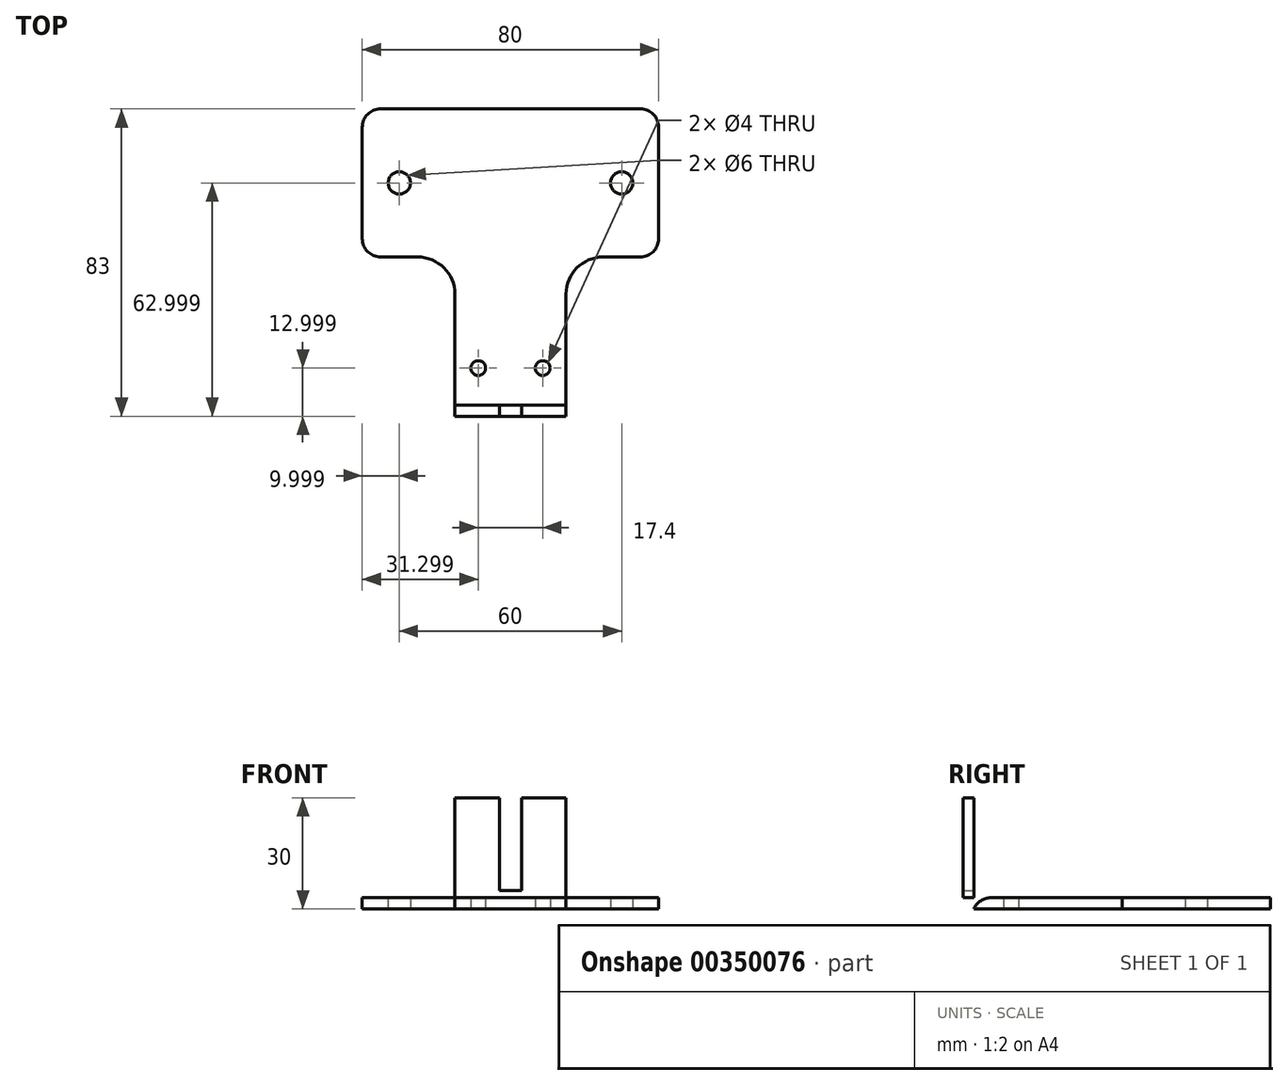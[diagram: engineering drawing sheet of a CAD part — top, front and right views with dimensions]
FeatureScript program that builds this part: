
annotation { "Feature Type Name" : "Feature", "Feature Type Description" : "" }
export const myFeature = defineFeature(function(context is Context, id is Id, definition is map)
    precondition{}
    {
        {
            var Q0;
            Q0=qCreatedBy(makeId("Top.planeOp"),FACE);
            var sketch = newSketch(context, id + "F0", { "sketchPlane" : qUnion([Q0])});
            skLineSegment(sketch, "E0.bottom", {"start": v(-29.94, -2.33) * mm, "end": v(40.06, -2.33) * mm});
            skLineSegment(sketch, "E0.top", {"start": v(-29.94, -42.33) * mm, "end": v(-19.94, -42.33) * mm});
            skLineSegment(sketch, "E0.left", {"start": v(-34.94, -7.33) * mm, "end": v(-34.94, -37.33) * mm});
            skLineSegment(sketch, "E0.right", {"start": v(45.06, -7.33) * mm, "end": v(45.06, -37.33) * mm});
            skLineSegment(sketch, "E1", {"start": v(-34.94, -22.33) * mm, "end": v(45.06, -22.33) * mm, "construction": true});
            skLineSegment(sketch, "E2", {"start": v(5.06, -2.33) * mm, "end": v(5.06, -42.33) * mm, "construction": true});
            skPoint(sketch, "E3", {"position": v(-24.94, -22.33) * mm});
            skPoint(sketch, "E4", {"position": v(35.06, -22.33) * mm});
            skLineSegment(sketch, "E5", {"start": v(5.06, -42.33) * mm, "end": v(5.06, -109.65) * mm, "construction": true});
            skLineSegment(sketch, "E6", {"start": v(-9.94, -52.33) * mm, "end": v(-9.94, -82.33) * mm});
            skLineSegment(sketch, "E7", {"start": v(-9.94, -82.33) * mm, "end": v(5.06, -82.33) * mm});
            skLineSegment(sketch, "E8.MirrorCS", {"start": v(20.06, -52.33) * mm, "end": v(20.06, -82.33) * mm});
            skLineSegment(sketch, "E9.MirrorCS", {"start": v(20.06, -82.33) * mm, "end": v(5.06, -82.33) * mm});
            skLineSegment(sketch, "E10.trimOffspring", {"start": v(30.06, -42.33) * mm, "end": v(40.06, -42.33) * mm});
            skPoint(sketch, "E11", {"position": v(-3.64, -72.33) * mm});
            skPoint(sketch, "E12", {"position": v(13.76, -72.33) * mm});
            skPoint(sketch, "E13.visualSharp", {"position": v(-34.94, -2.33) * mm});
            skArc(sketch, "E13.filletArc", {"start": v(-29.94, -2.33) * mm, "mid": v(-33.48, -3.8) * mm, "end": v(-34.94, -7.33) * mm});
            skPoint(sketch, "E14.visualSharp", {"position": v(45.06, -2.33) * mm});
            skArc(sketch, "E14.filletArc", {"start": v(45.06, -7.33) * mm, "mid": v(43.6, -3.8) * mm, "end": v(40.06, -2.33) * mm});
            skPoint(sketch, "E15.visualSharp", {"position": v(45.06, -42.33) * mm});
            skArc(sketch, "E15.filletArc", {"start": v(40.06, -42.33) * mm, "mid": v(43.6, -40.87) * mm, "end": v(45.06, -37.33) * mm});
            skPoint(sketch, "E16.visualSharp", {"position": v(20.06, -42.33) * mm});
            skArc(sketch, "E16.filletArc", {"start": v(30.06, -42.33) * mm, "mid": v(22.99, -45.26) * mm, "end": v(20.06, -52.33) * mm});
            skPoint(sketch, "E17.visualSharp", {"position": v(-34.94, -42.33) * mm});
            skArc(sketch, "E17.filletArc", {"start": v(-34.94, -37.33) * mm, "mid": v(-33.48, -40.87) * mm, "end": v(-29.94, -42.33) * mm});
            skPoint(sketch, "E18.visualSharp", {"position": v(-9.94, -42.33) * mm});
            skArc(sketch, "E18.filletArc", {"start": v(-9.94, -52.33) * mm, "mid": v(-12.87, -45.26) * mm, "end": v(-19.94, -42.33) * mm});
            skPoint(sketch, "E19.visualSharp", {"position": v(-9.94, -82.33) * mm});
            skLineSegment(sketch, "E19.filletArc", {"start": v(-9.94, -82.33) * mm, "end": v(-9.94, -82.33) * mm});
            skPoint(sketch, "E20.visualSharp", {"position": v(20.06, -82.33) * mm});
            skLineSegment(sketch, "E20.filletArc", {"start": v(20.06, -82.33) * mm, "end": v(20.06, -82.33) * mm});
            skSolve(sketch);
        }
        {
            var Q0;
            Q0=makeQuery(id+"F0.imprint","IMPRINT",FACE,{"disambiguationData":[TD([[makeQuery(id+"F0.imprint","IMPRINT",EDGE,{"derivedFrom":sQuery(id+"F0.wireOp",EDGE,"E0.bottom")}),-1.0]])]});
            extrude(context, id + "F1", {"entities" : qUnion([Q0]), "depth" : 3 * mm});
        }
        {
            var Q0;
            Q0=sQuery(id+"F0.wireOp",VERTEX,"E11");
            var Q1;
            Q1=sQuery(id+"F0.wireOp",VERTEX,"E12");
            var Q2;
            Q2=makeQuery(id+"F1.opExtrude","SWEPT_BODY",BODY,{"disambiguationData":[OSD([sQuery(id+"F0.wireOp",EDGE,"E0.bottom"),sQuery(id+"F0.wireOp",EDGE,"E0.top"),sQuery(id+"F0.wireOp",EDGE,"E0.left"),sQuery(id+"F0.wireOp",EDGE,"E0.right"),sQuery(id+"F0.wireOp",EDGE,"E6"),sQuery(id+"F0.wireOp",EDGE,"E7"),sQuery(id+"F0.wireOp",EDGE,"E8.MirrorCS"),sQuery(id+"F0.wireOp",EDGE,"E9.MirrorCS"),sQuery(id+"F0.wireOp",EDGE,"E10.trimOffspring")])]});
            hole(context, id + "F2", {"style" : HoleStyle.SIMPLE, "endStyle" : HoleEndStyle.THROUGH, "oppositeDirection" : true, "holeDiameter" : 4 * mm, "isTappedThrough" : true, "tappedDepth" : 12 * mm, "tapClearance" : 3, "locations" : qUnion([Q0, Q1]), "scope" : qUnion([Q2])});
        }
        {
            var Q0;
            Q0=sQuery(id+"F0.wireOp",VERTEX,"E3");
            var Q1;
            Q1=sQuery(id+"F0.wireOp",VERTEX,"E4");
            var Q2;
            Q2=makeQuery(id+"F1.opExtrude","SWEPT_BODY",BODY,{"disambiguationData":[OSD([sQuery(id+"F0.wireOp",EDGE,"E0.bottom"),sQuery(id+"F0.wireOp",EDGE,"E0.top"),sQuery(id+"F0.wireOp",EDGE,"E0.left"),sQuery(id+"F0.wireOp",EDGE,"E0.right"),sQuery(id+"F0.wireOp",EDGE,"E6"),sQuery(id+"F0.wireOp",EDGE,"E7"),sQuery(id+"F0.wireOp",EDGE,"E8.MirrorCS"),sQuery(id+"F0.wireOp",EDGE,"E9.MirrorCS"),sQuery(id+"F0.wireOp",EDGE,"E10.trimOffspring")])]});
            hole(context, id + "F3", {"style" : HoleStyle.SIMPLE, "endStyle" : HoleEndStyle.THROUGH, "oppositeDirection" : true, "holeDiameter" : 6 * mm, "isTappedThrough" : true, "tappedDepth" : 12 * mm, "tapClearance" : 3, "locations" : qUnion([Q0, Q1]), "scope" : qUnion([Q2])});
        }
        {
            var Q0;
            Q0=qCreatedBy(makeId("Top.planeOp"),FACE);
            cPlane(context, id + "F4", {"entities" : qUnion([Q0]), "cplaneType" : CPlaneType.OFFSET, "offset" : 100 * mm, "width" : 150 * mm, "height" : 150 * mm});
        }
        {
            var Q0;
            Q0=makeQuery(id+"F1.opExtrude","SWEPT_FACE",FACE,{"disambiguationData":[OSD([sQuery(id+"F0.wireOp",EDGE,"E7"),sQuery(id+"F0.wireOp",EDGE,"E9.MirrorCS")])]});
            var sketch = newSketch(context, id + "F5", { "sketchPlane" : qUnion([Q0])});
            skLineSegment(sketch, "E21.bottom", {"start": v(-9.94, 0) * mm, "end": v(20.06, 0) * mm});
            skLineSegment(sketch, "E21.top", {"start": v(-9.94, 30) * mm, "end": v(2.06, 30) * mm});
            skLineSegment(sketch, "E21.left", {"start": v(-9.94, 0) * mm, "end": v(-9.94, 30) * mm});
            skLineSegment(sketch, "E21.right", {"start": v(20.06, 0) * mm, "end": v(20.06, 30) * mm});
            skLineSegment(sketch, "E22", {"start": v(5.06, 0) * mm, "end": v(5.06, 30) * mm, "construction": true});
            skLineSegment(sketch, "E23", {"start": v(2.06, 30) * mm, "end": v(2.06, 5) * mm});
            skLineSegment(sketch, "E24", {"start": v(2.06, 5) * mm, "end": v(8.06, 5) * mm});
            skLineSegment(sketch, "E25", {"start": v(8.06, 5) * mm, "end": v(8.06, 30) * mm});
            skLineSegment(sketch, "E26.trimOffspring", {"start": v(8.06, 30) * mm, "end": v(20.06, 30) * mm});
            skSolve(sketch);
        }
        {
            var Q0;
            {var subQ0=sQuery(id+"F5.wireOp",EDGE,"E21.top");Q0=makeQuery(id+"F5.imprint","IMPRINT",FACE,{"disambiguationData":[TD([[makeQuery(id+"F5.imprint","IMPRINT",EDGE,{"derivedFrom":subQ0}),-1.0]])]});}
            var Q1;
            {var subQ5=sQuery(id+"F5.wireOp",EDGE,"E21.bottom");Q1=makeQuery(id+"F5.imprint","IMPRINT",FACE,{"disambiguationData":[TD([[makeQuery(id+"F5.imprint","IMPRINT",EDGE,{"derivedFrom":subQ5}),-1.0]])]});}
            var Q2;
            {var subQ3=sQuery(id+"F5.wireOp",EDGE,"E26.trimOffspring");Q2=makeQuery(id+"F5.imprint","IMPRINT",FACE,{"disambiguationData":[TD([[makeQuery(id+"F5.imprint","IMPRINT",EDGE,{"derivedFrom":subQ3}),-1.0]])]});}
            extrude(context, id + "F6", {"entities" : qUnion([Q0, Q1, Q2]), "operationType" : NewBodyOperationType.ADD, "depth" : 3 * mm});
        }
        {
            var Q0;
            Q0=makeQuery(id+"F1.opExtrude","CAP_EDGE",EDGE,{"disambiguationData":[OSD([sQuery(id+"F0.wireOp",EDGE,"E7"),sQuery(id+"F0.wireOp",EDGE,"E9.MirrorCS")])],"isStart":false});
            var Q1;
            Q1=makeQuery(id+"F6.opExtrude","CAP_EDGE",EDGE,{"disambiguationData":[OSD([sQuery(id+"F5.wireOp",EDGE,"E21.bottom")])],"isStart":false});
            fillet(context, id + "F7", {"entities" : qUnion([Q0, Q1]), "radius" : 5 * mm, "tangentPropagation" : true, "allowEdgeOverflow" : false});
        }
    });
